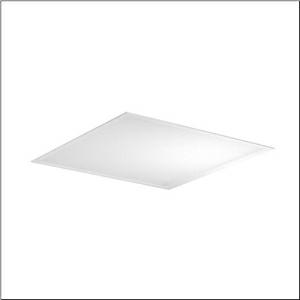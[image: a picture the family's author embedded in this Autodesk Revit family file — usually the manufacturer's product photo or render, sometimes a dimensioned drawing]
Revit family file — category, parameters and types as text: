
# Revit family: apollon_21_square_51mq12wd2114
name_source: partatom
category: Lighting Fixtures
units: mm (PartAtom-declared; Revit-internal decimal feet)

## family parameters
Cut with Voids When Loaded = No
Host = Face
Light Source = No
Part Type = Normal
Room Calculation Point = No
Round Connector Dimension = Use Diameter
Shared = No

## types (1)
- Apollon 21 square (1 x LED, 4100 lm, 24.7 W, 4000K)
    Apparent Load = 25 VA
    CIE Flux Codes = 60 87 97 100 100
    Color Rendering = 90
    Color Temperature = 4000K
    Default Elevation = 1800 mm
    Description = Apollon 21 square, office luminaire, primary optical cover: micro prismatic cover, of PMMA, CAT 2 (L<= 3000cd/m²), light emission: direct distribution, primary light characteristic: symmetric, installation type: lay-in mounting, LED, rated luminous flux: 4.100lm, luminous efficacy: 166lm/W, light colour: 940, colour temperature: 4000K, control gear: DALI 2, Multilumen, with terminal, 5-pole, mains connection: 220..240V, AC/DC, 0/50..60Hz, rated input power: 24.7W, housing, of aluminium, coated, traffic white (RAL 9016), module: M600, length: 595mm, width: 595mm, height: 55mm, recess depth: 180mm, housing upper side, of sheet steel, galvanised, protection rating (complete): IP20, protection rating (lamp compartment, on room side): IP50, insulation class (complete): insulation class II (safety insulation), certification: CE, ENEC, impact resistance: IK03, permissible operating ambient temperature: -20..+45°C, permissible storage temperature: -40..+80°C, standard: EN 60598-2-22, packaging unit: 1 piece
    Height = 0 mm  [stored 0 ft]
    Lamp = 1 x LED
    Lamp Light Flux = 4100 lm
    Lamp Power = 24.7 W
    Lamp count = 1
    Length = 595 mm
    Luminous efficacy = 166 lm/W
    Manufacturer = Siteco
    ModVariant = No
    Model = 51MQ12WD2114
    Mounting Place = Ceiling
    Mounting Type = Recessed
    Number of Poles = 1
    OnlyDefault = Yes
    Power Factor = 1
    Product Name = Apollon 21 square
    Product group = office luminaire | ceiling recessed
    ProductGroupID = 401
    Protection Class = Protection class II
    Protection Degree = IP 20
    RLX_Detail_Level = 1
    RLX_Emergency_Light_Flux = 0 lm
    RLX_Emergency_Type = 0
    RLX_Emergency_Type_DB = No
    RlxData = <blob elided: 12565 chars, md5=f4ede25b>
    Socket = socket
    Standby Power = 0 W
    System Light Flux = 4100 lm
    System Power = 25 W
    Type Comments = Product without accessories
    Type Image = l_1291049.jpg
    URL = http://relux.com
    VarID = ---
    Voltage = 0 V
    Weight = 0.00 kg
    Width = 595 mm

note: [stored X ft] marks values corroborated as IEEE doubles in the binary element streams (Revit-internal decimal feet)

## geometry (parser evidence)
native form markers: Sweep x9
no freeform markers — native parametric forms only
